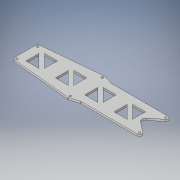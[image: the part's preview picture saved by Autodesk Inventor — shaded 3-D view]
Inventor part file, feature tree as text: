
AUTODESK INVENTOR PART (.ipt)
format: ipt  version: 2019 (Build 230136000, 136)  size: 206,848 bytes
history: native  units: mm
features: other x1, extrude x1, sketch x1
ambient origin geometry x8: Origin, YZ Plane, XZ Plane, XY Plane, X Axis, Y Axis, Z Axis, Center Point
bodies: Body1 (feature_tree)
feature tree (3):
  other  "Bryła1"
  extrude  "Wyciągnięcie proste1"  Depth=29.0mm
  sketch  "Szkic2"
